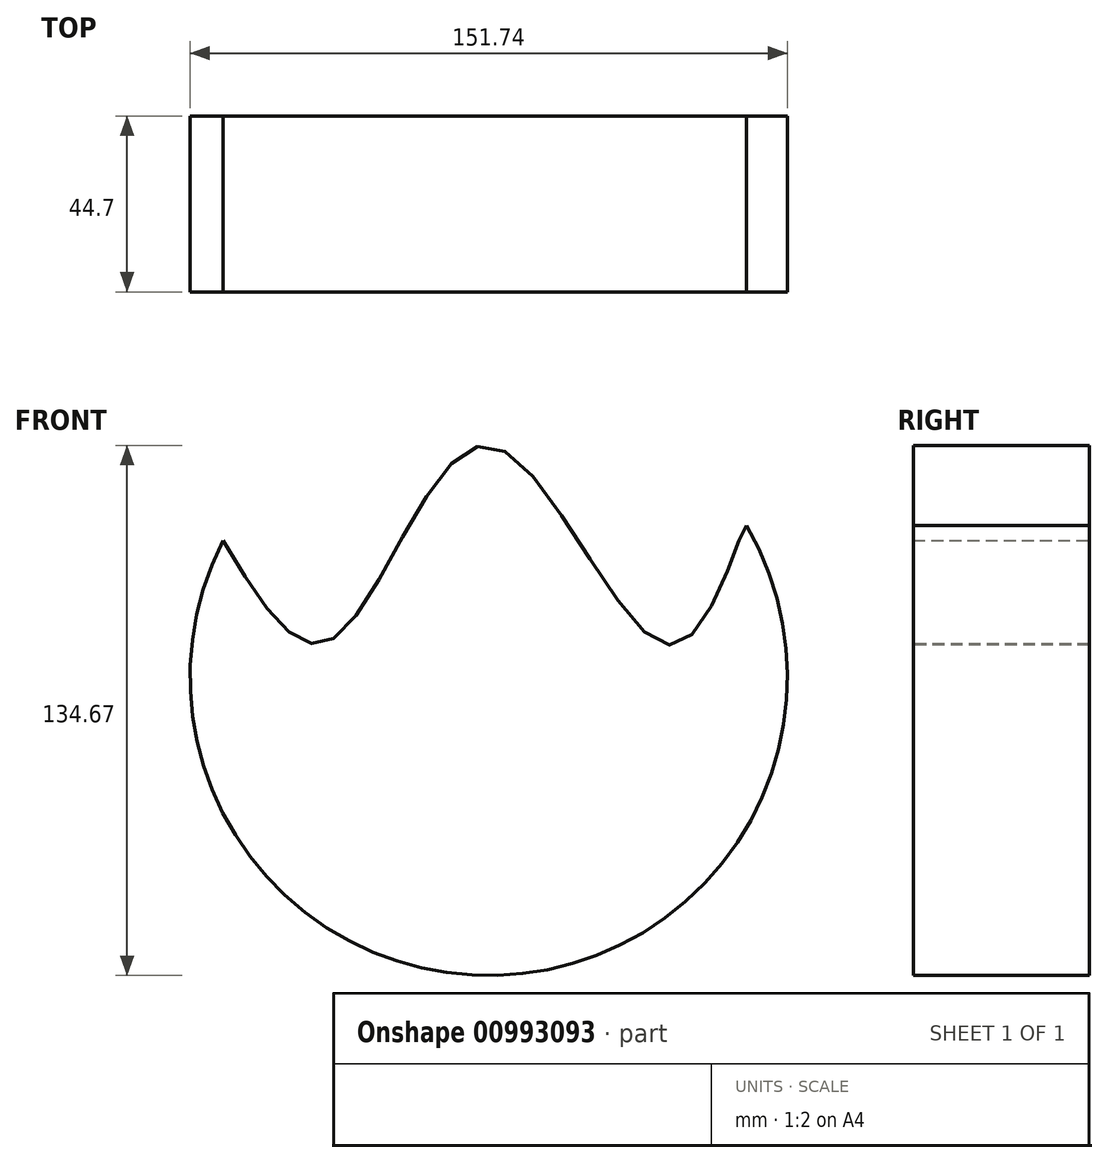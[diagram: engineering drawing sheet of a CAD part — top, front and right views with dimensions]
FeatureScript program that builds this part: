
annotation { "Feature Type Name" : "Feature", "Feature Type Description" : "" }
export const myFeature = defineFeature(function(context is Context, id is Id, definition is map)
    precondition{}
    {
        {
            var Q0;
            Q0=qCreatedBy(makeId("Front.planeOp"),FACE);
            var sketch = newSketch(context, id + "F0", { "sketchPlane" : qUnion([Q0])});
            skCircle(sketch, "E0", {"center": v(0, 0) * mm, "radius": 75.87 * mm});
            skFitSpline(sketch, "E1", {"points": [v(-67.52, 34.62) * mm, v(-39.53, 9.62) * mm, v(0, 58.76) * mm, v(46.86, 8.09) * mm, v(65.43, 38.42) * mm, v(66.1, 37.24) * mm], "startDerivative": vector(133.76, -222.42) * mm, "endDerivative": vector(10.6, -56) * mm});
            skSolve(sketch);
        }
        {
            var Q0;
            Q0=makeQuery(id+"F0.imprint","IMPRINT",FACE,{"disambiguationData":[TD([[makeQuery(id+"F0.imprint","IMPRINT",EDGE,{"derivedFrom":sQuery(id+"F0.wireOp",EDGE,"E0")}),1.0]])]});
            extrude(context, id + "F1", {"entities" : qUnion([Q0]), "depth" : 44.45 * mm, "offsetDistance" : 25.4 * mm});
        }
        {
            var Q0;
            Q0=makeQuery(id+"F1.opExtrude","CAP_FACE",FACE,{"disambiguationData":[OSD([sQuery(id+"F0.wireOp",EDGE,"E0"),sQuery(id+"F0.wireOp",EDGE,"E1")])],"isStart":false});
            extrude(context, id + "F2", {"entities" : qUnion([Q0]), "operationType" : NewBodyOperationType.ADD, "depth" : 0.25 * mm, "offsetDistance" : 25.4 * mm});
        }
    });
